# Revit family: Winkel 40-5 4-Loch 135°, VA neu
name_source: partatom
category: HLS-Bauteile
revit_build: Autodesk Revit 2017 (Build: 20190507_1515(x64)
units: mm (PartAtom-declared; Revit-internal decimal feet)

## family parameters
Arbeitsebenenbasiert = Ja
Beim Laden mit Abzugskörper schneiden = Nein
Bemaßung runder Anschluss = Durchmesser verwenden
Gemeinsam genutzt = Ja
Immer vertikal = Nein
Raumberechnungspunkt = Nein
Teiletyp = Normal

## types (2) — shared parameters
B = 40 mm  [stored 0.131234 ft]
Fabrikat = MEFA
Firma = MEFA Befestigungs- und Montagesysteme GmbH
Gewicht = 0.00 kg
Gewicht pro Bauteil = 0.00 kg
L1 = 103 mm
L2 = 103 mm
Lochdurchmesser = 13 mm
Material = Edelstahl
Profil = C-Profil
Profiltyp = 45
S = 5 mm  [stored 0.0164042 ft]
Stärke Material = 5 mm  [stored 0.0164042 ft]
Vorgabe-Ansicht = 1219 mm
Winkel 1 = 135.00°
max. zul. Last mit Profil = 0.00 kN
max. zul. Last ohne Profil = 0.00 kN
zero-valued in all types: Breite Schenkel, Länge Schenkel

## per-type parameters (varying)
| type | Artikelnummer | Kurztext1 |
| Winkel 40-5 4-Loch 135°, V2A | 048040601 | Winkel 4-Lo. C-Profil 45 V2A |
| Winkel 40-5 4-Loch 135°, V4A | 048140601 | Winkel 4-Lo. C-Profil 45 V4A |

note: [stored X ft] marks values corroborated as IEEE doubles in the binary element streams (Revit-internal decimal feet)
